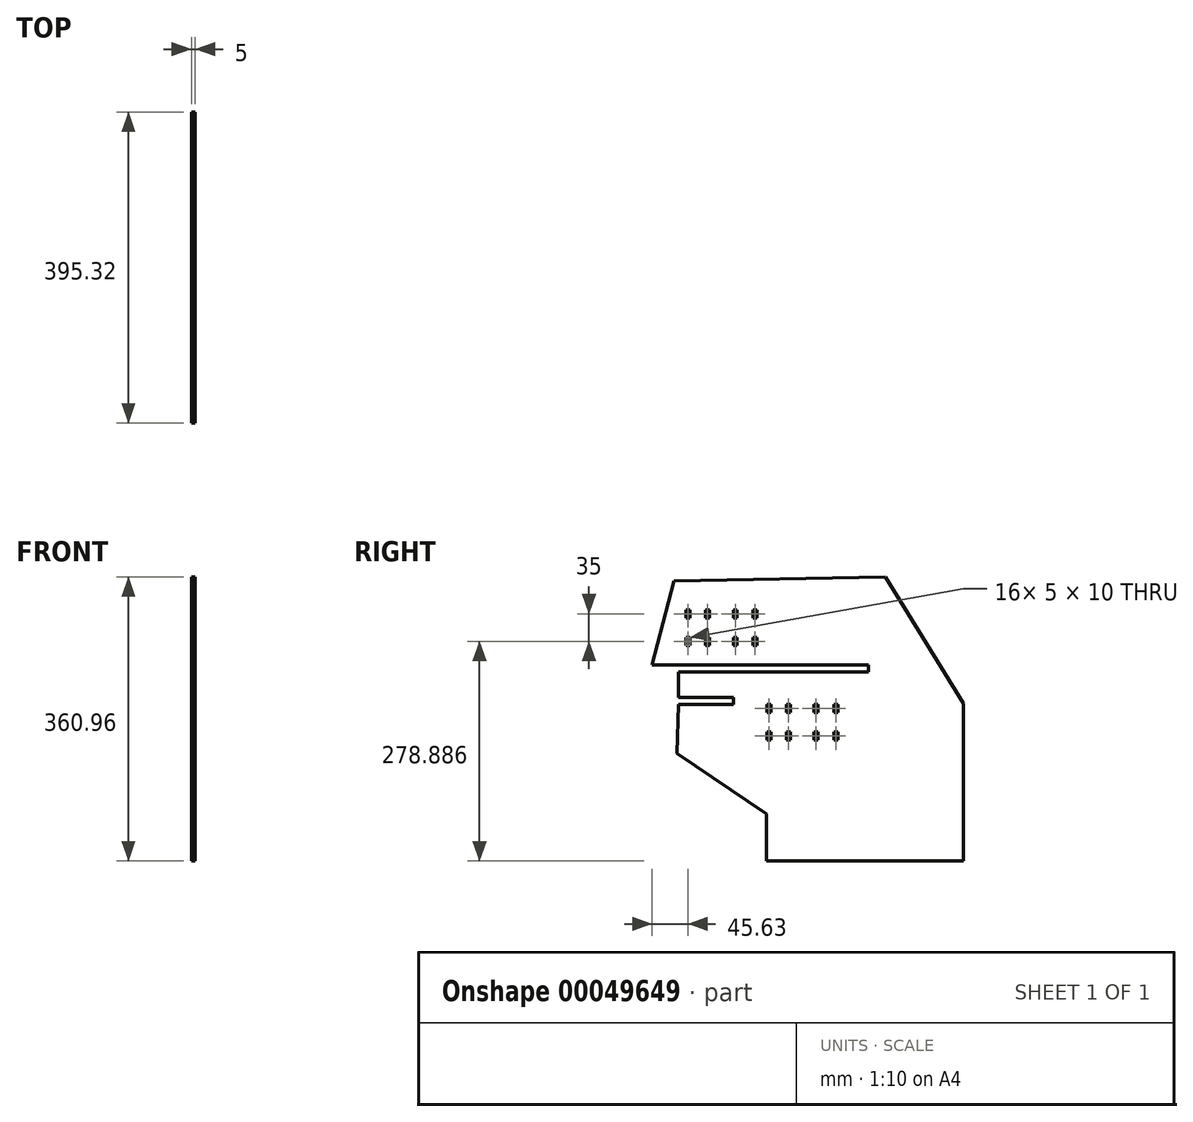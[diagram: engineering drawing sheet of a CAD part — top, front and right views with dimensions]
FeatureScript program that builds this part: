
annotation { "Feature Type Name" : "Feature", "Feature Type Description" : "" }
export const myFeature = defineFeature(function(context is Context, id is Id, definition is map)
    precondition{}
    {
        {
            var Q0;
            Q0=qCreatedBy(makeId("Right.planeOp"),FACE);
            var sketch = newSketch(context, id + "F0", { "sketchPlane" : qUnion([Q0])});
            skLineSegment(sketch, "E0.bottom", {"start": v(0, 0) * mm, "end": v(250, 0) * mm});
            skLineSegment(sketch, "E0.left", {"start": v(0, 0) * mm, "end": v(0, 59.53) * mm});
            skLineSegment(sketch, "E0.right", {"start": v(250, 0) * mm, "end": v(250, 200) * mm});
            skLineSegment(sketch, "E1.top", {"start": v(-41.98, 198.89) * mm, "end": v(-111.98, 198.89) * mm});
            skLineSegment(sketch, "E1.right", {"start": v(-113.68, 136.74) * mm, "end": v(-111.98, 198.89) * mm});
            skLineSegment(sketch, "E2.bottom", {"start": v(129.49, 239.89) * mm, "end": v(-111.98, 239.89) * mm});
            skLineSegment(sketch, "E2.top", {"start": v(-41.98, 207.89) * mm, "end": v(-111.98, 207.89) * mm});
            skLineSegment(sketch, "E2.right", {"start": v(-111.98, 207.89) * mm, "end": v(-111.98, 239.89) * mm});
            skLineSegment(sketch, "E3", {"start": v(-113.68, 136.74) * mm, "end": v(0, 59.53) * mm});
            skLineSegment(sketch, "E4", {"start": v(129.49, 239.89) * mm, "end": v(129.49, 248.89) * mm});
            skLineSegment(sketch, "E5", {"start": v(129.49, 248.89) * mm, "end": v(-145.32, 248.89) * mm});
            skLineSegment(sketch, "E6", {"start": v(-145.32, 248.89) * mm, "end": v(-117.49, 355.6) * mm});
            skLineSegment(sketch, "E7", {"start": v(-117.49, 355.6) * mm, "end": v(151.16, 360.96) * mm});
            skLineSegment(sketch, "E8", {"start": v(151.16, 360.96) * mm, "end": v(250, 200) * mm});
            skLineSegment(sketch, "E9.trimOffspring", {"start": v(-41.98, 198.89) * mm, "end": v(-41.98, 207.89) * mm});
            skLineSegment(sketch, "E10", {"start": v(-42.2, 357.1) * mm, "end": v(-42.2, 248.89) * mm, "construction": true});
            skLineSegment(sketch, "E11.bottom", {"start": v(-42.2, 308.89) * mm, "end": v(-37.2, 308.89) * mm});
            skLineSegment(sketch, "E11.top", {"start": v(-42.2, 318.89) * mm, "end": v(-37.2, 318.89) * mm});
            skLineSegment(sketch, "E11.left", {"start": v(-42.2, 308.89) * mm, "end": v(-42.2, 318.89) * mm});
            skLineSegment(sketch, "E11.right", {"start": v(-37.2, 308.89) * mm, "end": v(-37.2, 318.89) * mm});
            skLineSegment(sketch, "E12.bottom", {"start": v(-42.2, 283.89) * mm, "end": v(-37.2, 283.89) * mm});
            skLineSegment(sketch, "E12.top", {"start": v(-42.2, 273.89) * mm, "end": v(-37.2, 273.89) * mm});
            skLineSegment(sketch, "E12.left", {"start": v(-42.2, 283.89) * mm, "end": v(-42.2, 273.89) * mm});
            skLineSegment(sketch, "E12.right", {"start": v(-37.2, 283.89) * mm, "end": v(-37.2, 273.89) * mm});
            skLineSegment(sketch, "E13", {"start": v(-77.2, 248.89) * mm, "end": v(-77.2, 356.4) * mm, "construction": true});
            skLineSegment(sketch, "E14.bottom", {"start": v(-77.2, 318.89) * mm, "end": v(-72.2, 318.89) * mm});
            skLineSegment(sketch, "E14.top", {"start": v(-77.2, 308.89) * mm, "end": v(-72.2, 308.89) * mm});
            skLineSegment(sketch, "E14.left", {"start": v(-77.2, 318.89) * mm, "end": v(-77.2, 308.89) * mm});
            skLineSegment(sketch, "E14.right", {"start": v(-72.2, 318.89) * mm, "end": v(-72.2, 308.89) * mm});
            skLineSegment(sketch, "E15.bottom", {"start": v(-77.2, 283.89) * mm, "end": v(-72.2, 283.89) * mm});
            skLineSegment(sketch, "E15.top", {"start": v(-77.2, 273.89) * mm, "end": v(-72.2, 273.89) * mm});
            skLineSegment(sketch, "E15.left", {"start": v(-77.2, 283.89) * mm, "end": v(-77.2, 273.89) * mm});
            skLineSegment(sketch, "E15.right", {"start": v(-72.2, 283.89) * mm, "end": v(-72.2, 273.89) * mm});
            skLineSegment(sketch, "E16.bottom", {"start": v(-97.2, 318.89) * mm, "end": v(-102.2, 318.89) * mm});
            skLineSegment(sketch, "E16.top", {"start": v(-97.2, 308.89) * mm, "end": v(-102.2, 308.89) * mm});
            skLineSegment(sketch, "E16.left", {"start": v(-97.2, 318.89) * mm, "end": v(-97.2, 308.89) * mm});
            skLineSegment(sketch, "E16.right", {"start": v(-102.2, 318.89) * mm, "end": v(-102.2, 308.89) * mm});
            skLineSegment(sketch, "E17.bottom", {"start": v(-97.2, 283.89) * mm, "end": v(-102.2, 283.89) * mm});
            skLineSegment(sketch, "E17.top", {"start": v(-97.2, 273.89) * mm, "end": v(-102.2, 273.89) * mm});
            skLineSegment(sketch, "E17.left", {"start": v(-97.2, 283.89) * mm, "end": v(-97.2, 273.89) * mm});
            skLineSegment(sketch, "E17.right", {"start": v(-102.2, 283.89) * mm, "end": v(-102.2, 273.89) * mm});
            skLineSegment(sketch, "E18", {"start": v(-102.2, 248.89) * mm, "end": v(-102.2, 355.9) * mm, "construction": true});
            skLineSegment(sketch, "E19", {"start": v(-17.2, 357.6) * mm, "end": v(-17.2, 248.89) * mm, "construction": true});
            skLineSegment(sketch, "E20.bottom", {"start": v(-17.2, 318.89) * mm, "end": v(-12.2, 318.89) * mm});
            skLineSegment(sketch, "E20.top", {"start": v(-17.2, 308.89) * mm, "end": v(-12.2, 308.89) * mm});
            skLineSegment(sketch, "E20.left", {"start": v(-17.2, 318.89) * mm, "end": v(-17.2, 308.89) * mm});
            skLineSegment(sketch, "E20.right", {"start": v(-12.2, 318.89) * mm, "end": v(-12.2, 308.89) * mm});
            skLineSegment(sketch, "E21.bottom", {"start": v(-17.2, 283.89) * mm, "end": v(-12.2, 283.89) * mm});
            skLineSegment(sketch, "E21.top", {"start": v(-17.2, 273.89) * mm, "end": v(-12.2, 273.89) * mm});
            skLineSegment(sketch, "E21.left", {"start": v(-17.2, 283.89) * mm, "end": v(-17.2, 273.89) * mm});
            skLineSegment(sketch, "E21.right", {"start": v(-12.2, 283.89) * mm, "end": v(-12.2, 273.89) * mm});
            skLineSegment(sketch, "E22", {"start": v(0.53, 239.89) * mm, "end": v(0.53, 101.8) * mm, "construction": true});
            skLineSegment(sketch, "E23", {"start": v(25.53, 239.89) * mm, "end": v(25.53, 93.87) * mm, "construction": true});
            skLineSegment(sketch, "E24.bottom", {"start": v(0.53, 198.63) * mm, "end": v(5.53, 198.63) * mm});
            skLineSegment(sketch, "E24.top", {"start": v(0.53, 188.63) * mm, "end": v(5.53, 188.63) * mm});
            skLineSegment(sketch, "E24.left", {"start": v(0.53, 198.63) * mm, "end": v(0.53, 188.63) * mm});
            skLineSegment(sketch, "E24.right", {"start": v(5.53, 198.63) * mm, "end": v(5.53, 188.63) * mm});
            skLineSegment(sketch, "E25.bottom", {"start": v(25.53, 198.63) * mm, "end": v(30.53, 198.63) * mm});
            skLineSegment(sketch, "E25.top", {"start": v(25.53, 188.63) * mm, "end": v(30.53, 188.63) * mm});
            skLineSegment(sketch, "E25.left", {"start": v(25.53, 198.63) * mm, "end": v(25.53, 188.63) * mm});
            skLineSegment(sketch, "E25.right", {"start": v(30.53, 198.63) * mm, "end": v(30.53, 188.63) * mm});
            skLineSegment(sketch, "E26.bottom", {"start": v(0.53, 163.63) * mm, "end": v(5.53, 163.63) * mm});
            skLineSegment(sketch, "E26.top", {"start": v(0.53, 153.63) * mm, "end": v(5.53, 153.63) * mm});
            skLineSegment(sketch, "E26.left", {"start": v(0.53, 163.63) * mm, "end": v(0.53, 153.63) * mm});
            skLineSegment(sketch, "E26.right", {"start": v(5.53, 163.63) * mm, "end": v(5.53, 153.63) * mm});
            skLineSegment(sketch, "E27.bottom", {"start": v(25.53, 163.63) * mm, "end": v(30.53, 163.63) * mm});
            skLineSegment(sketch, "E27.top", {"start": v(25.53, 153.63) * mm, "end": v(30.53, 153.63) * mm});
            skLineSegment(sketch, "E27.left", {"start": v(25.53, 163.63) * mm, "end": v(25.53, 153.63) * mm});
            skLineSegment(sketch, "E27.right", {"start": v(30.53, 163.63) * mm, "end": v(30.53, 153.63) * mm});
            skLineSegment(sketch, "E28.1.0.0", {"start": v(85.53, 188.63) * mm, "end": v(90.53, 188.63) * mm});
            skLineSegment(sketch, "E28.1.0.1", {"start": v(90.53, 198.63) * mm, "end": v(90.53, 188.63) * mm});
            skLineSegment(sketch, "E28.1.0.2", {"start": v(85.53, 198.63) * mm, "end": v(90.53, 198.63) * mm});
            skLineSegment(sketch, "E28.1.0.3", {"start": v(85.53, 198.63) * mm, "end": v(85.53, 188.63) * mm});
            skLineSegment(sketch, "E28.1.0.4", {"start": v(65.53, 198.63) * mm, "end": v(65.53, 188.63) * mm});
            skLineSegment(sketch, "E28.1.0.5", {"start": v(60.53, 198.63) * mm, "end": v(65.53, 198.63) * mm});
            skLineSegment(sketch, "E28.1.0.6", {"start": v(60.53, 198.63) * mm, "end": v(60.53, 188.63) * mm});
            skLineSegment(sketch, "E28.1.0.7", {"start": v(60.53, 188.63) * mm, "end": v(65.53, 188.63) * mm});
            skLineSegment(sketch, "E28.1.0.8", {"start": v(65.53, 163.63) * mm, "end": v(65.53, 153.63) * mm});
            skLineSegment(sketch, "E28.1.0.9", {"start": v(60.53, 163.63) * mm, "end": v(65.53, 163.63) * mm});
            skLineSegment(sketch, "E28.1.0.10", {"start": v(60.53, 163.63) * mm, "end": v(60.53, 153.63) * mm});
            skLineSegment(sketch, "E28.1.0.11", {"start": v(60.53, 153.63) * mm, "end": v(65.53, 153.63) * mm});
            skLineSegment(sketch, "E28.1.0.12", {"start": v(85.53, 163.63) * mm, "end": v(85.53, 153.63) * mm});
            skLineSegment(sketch, "E28.1.0.13", {"start": v(85.53, 163.63) * mm, "end": v(90.53, 163.63) * mm});
            skLineSegment(sketch, "E28.1.0.14", {"start": v(85.53, 153.63) * mm, "end": v(90.53, 153.63) * mm});
            skLineSegment(sketch, "E28.1.0.15", {"start": v(90.53, 163.63) * mm, "end": v(90.53, 153.63) * mm});
            skSolve(sketch);
        }
        {
            var Q0;
            {var subQ3=sQuery(id+"F0.wireOp",EDGE,"E0.bottom");Q0=makeQuery(id+"F0.imprint","IMPRINT",FACE,{"disambiguationData":[TD([[makeQuery(id+"F0.imprint","IMPRINT",EDGE,{"derivedFrom":subQ3}),1.0]])]});}
            var Q1;
            Q1=makeQuery(id+"F0.imprint","IMPRINT",FACE,{"disambiguationData":[TD([[makeQuery(id+"F0.imprint","IMPRINT",EDGE,{"derivedFrom":sQuery(id+"F0.wireOp",EDGE,"E2.bottom")}),-1.0]])]});
            var Q2;
            Q2=makeQuery(id+"F0.imprint","IMPRINT",FACE,{"disambiguationData":[TD([[makeQuery(id+"F0.imprint","IMPRINT",EDGE,{"derivedFrom":sQuery(id+"F0.wireOp",EDGE,"E1.bottom")}),-1.0]])]});
            var Q3;
            Q3=makeQuery(id+"F0.imprint","IMPRINT",FACE,{"disambiguationData":[TD([[makeQuery(id+"F0.imprint","IMPRINT",EDGE,{"derivedFrom":sQuery(id+"F0.wireOp",EDGE,"E1.top")}),1.0]])]});
            var Q4;
            Q4=makeQuery(id+"F0.imprint","IMPRINT",FACE,{"disambiguationData":[TD([[makeQuery(id+"F0.imprint","IMPRINT",EDGE,{"derivedFrom":sQuery(id+"F0.wireOp",EDGE,"E2.bottom")}),1.0]])]});
            extrude(context, id + "F1", {"entities" : qUnion([Q0, Q1, Q2, Q3, Q4]), "depth" : 5 * mm});
        }
    });
